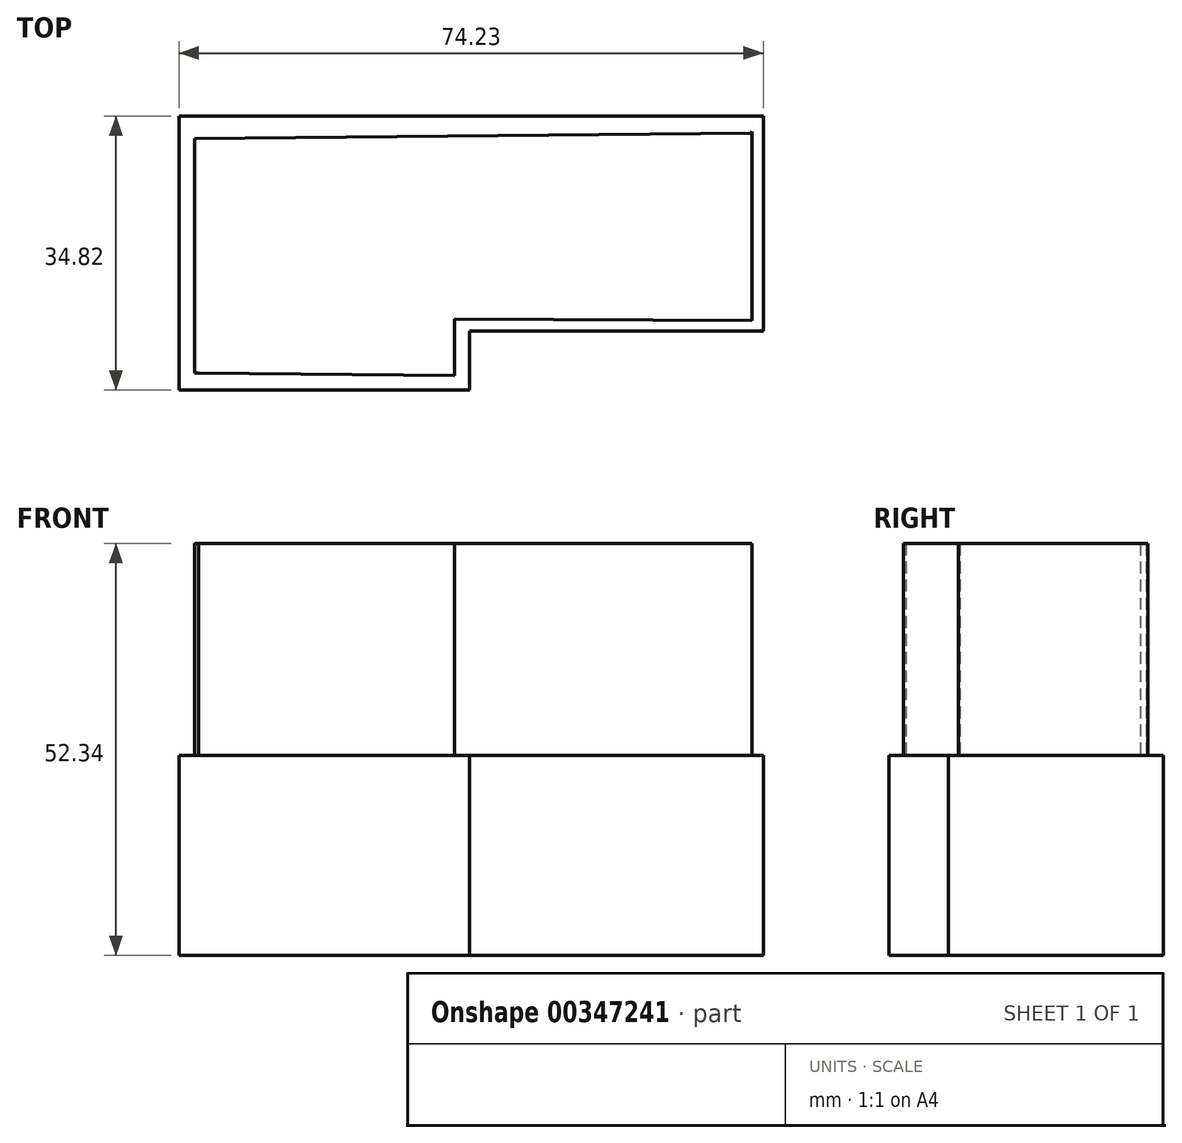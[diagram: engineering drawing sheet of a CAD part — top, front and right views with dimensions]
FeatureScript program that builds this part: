
annotation { "Feature Type Name" : "Feature", "Feature Type Description" : "" }
export const myFeature = defineFeature(function(context is Context, id is Id, definition is map)
    precondition{}
    {
        {
            var Q0;
            Q0=qCreatedBy(makeId("Top.planeOp"),FACE);
            var sketch = newSketch(context, id + "F0", { "sketchPlane" : qUnion([Q0])});
            skLineSegment(sketch, "E0.bottom", {"start": v(-41.96, -18.27) * mm, "end": v(-5.06, -18.27) * mm});
            skLineSegment(sketch, "E0.top", {"start": v(-41.96, -53.1) * mm, "end": v(-5.06, -53.1) * mm});
            skLineSegment(sketch, "E0.left", {"start": v(-41.96, -18.27) * mm, "end": v(-41.96, -53.1) * mm});
            skLineSegment(sketch, "E0.right", {"start": v(-5.06, -18.27) * mm, "end": v(-5.06, -53.1) * mm});
            skLineSegment(sketch, "E1.bottom", {"start": v(-5.06, -18.27) * mm, "end": v(-5.06, -18.27) * mm});
            skLineSegment(sketch, "E1.top", {"start": v(-5.06, -18.27) * mm, "end": v(-5.06, -18.27) * mm});
            skLineSegment(sketch, "E1.left", {"start": v(-5.06, -18.27) * mm, "end": v(-5.06, -18.27) * mm});
            skLineSegment(sketch, "E1.right", {"start": v(-5.06, -18.27) * mm, "end": v(-5.06, -18.27) * mm});
            skLineSegment(sketch, "E2.bottom", {"start": v(-5.06, -18.27) * mm, "end": v(32.27, -18.27) * mm});
            skLineSegment(sketch, "E2.top", {"start": v(-5.06, -45.58) * mm, "end": v(32.27, -45.58) * mm});
            skLineSegment(sketch, "E2.left", {"start": v(-5.06, -18.27) * mm, "end": v(-5.06, -45.58) * mm});
            skLineSegment(sketch, "E2.right", {"start": v(32.27, -18.27) * mm, "end": v(32.27, -45.58) * mm});
            skSolve(sketch);
        }
        {
            var Q0;
            Q0 = qSketchRegion(id + "F0", true);
            extrude(context, id + "F1", {"entities" : qUnion([Q0]), "depth" : 25.4 * mm});
        }
        {
            var Q0;
            Q0=makeQuery(id+"F1.opExtrude","CAP_FACE",FACE,{"disambiguationData":[OSD([sQuery(id+"F0.wireOp",EDGE,"E0.bottom"),sQuery(id+"F0.wireOp",EDGE,"E0.top"),sQuery(id+"F0.wireOp",EDGE,"E0.left"),sQuery(id+"F0.wireOp",EDGE,"E0.right"),sQuery(id+"F0.wireOp",EDGE,"E2.bottom"),sQuery(id+"F0.wireOp",EDGE,"E2.top"),sQuery(id+"F0.wireOp",EDGE,"E2.right")])],"isStart":false});
            var sketch = newSketch(context, id + "F2", { "sketchPlane" : qUnion([Q0])});
            skLineSegment(sketch, "E3", {"start": v(-39.95, -21.17) * mm, "end": v(-39.95, -50.94) * mm});
            skLineSegment(sketch, "E4", {"start": v(-39.95, -50.94) * mm, "end": v(-39.44, -50.93) * mm});
            skLineSegment(sketch, "E5", {"start": v(-39.44, -50.93) * mm, "end": v(-6.92, -51.26) * mm});
            skLineSegment(sketch, "E6", {"start": v(-6.92, -51.26) * mm, "end": v(-6.92, -44.1) * mm});
            skLineSegment(sketch, "E7", {"start": v(-6.92, -44.1) * mm, "end": v(30.81, -44.27) * mm});
            skLineSegment(sketch, "E8", {"start": v(30.81, -44.27) * mm, "end": v(30.81, -20.26) * mm});
            skLineSegment(sketch, "E9", {"start": v(30.81, -20.26) * mm, "end": v(30.7, -20.43) * mm});
            skLineSegment(sketch, "E10", {"start": v(30.7, -20.43) * mm, "end": v(-39.95, -21.17) * mm});
            skSolve(sketch);
        }
        {
            var Q0;
            Q0=makeQuery(id+"F2.imprint","IMPRINT",FACE,{"disambiguationData":[TD([[makeQuery(id+"F2.imprint","IMPRINT",EDGE,{"derivedFrom":sQuery(id+"F2.wireOp",EDGE,"E3")}),1.0]])]});
            extrude(context, id + "F3", {"entities" : qUnion([Q0]), "operationType" : NewBodyOperationType.ADD, "depth" : 26.94 * mm});
        }
    });
